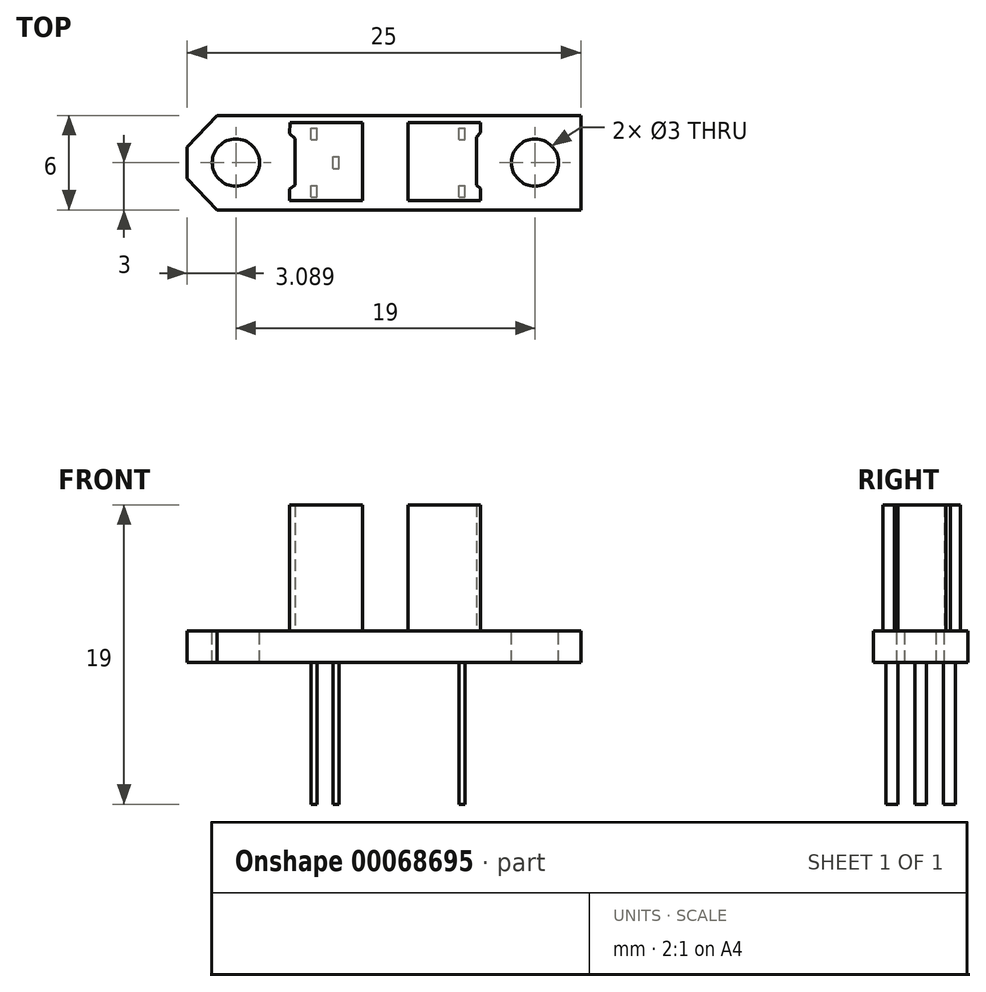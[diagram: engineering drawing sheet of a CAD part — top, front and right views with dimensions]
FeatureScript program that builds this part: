
annotation { "Feature Type Name" : "Feature", "Feature Type Description" : "" }
export const myFeature = defineFeature(function(context is Context, id is Id, definition is map)
    precondition{}
    {
        {
            var Q0;
            Q0=qCreatedBy(makeId("Top.planeOp"),FACE);
            var sketch = newSketch(context, id + "F0", { "sketchPlane" : qUnion([Q0])});
            skLineSegment(sketch, "E0.bottom", {"start": v(-23.1, 3) * mm, "end": v(0, 3) * mm});
            skLineSegment(sketch, "E0.top", {"start": v(-23.1, -3) * mm, "end": v(0, -3) * mm});
            skLineSegment(sketch, "E0.right", {"start": v(0, 3) * mm, "end": v(0, -3) * mm});
            skLineSegment(sketch, "E1", {"start": v(-23.1, 3) * mm, "end": v(-25, 1) * mm});
            skLineSegment(sketch, "E2", {"start": v(-25, 1) * mm, "end": v(-25, -1) * mm});
            skLineSegment(sketch, "E3", {"start": v(-25, -1) * mm, "end": v(-23.1, -3) * mm});
            skCircle(sketch, "E4", {"center": v(-21.91, 0) * mm, "radius": 1.5 * mm});
            skCircle(sketch, "E5", {"center": v(-2.91, 0) * mm, "radius": 1.5 * mm});
            skLineSegment(sketch, "E6", {"start": v(-18.47, 2.54) * mm, "end": v(-13.86, 2.54) * mm});
            skLineSegment(sketch, "E7", {"start": v(-13.86, 2.54) * mm, "end": v(-13.86, -2.4) * mm});
            skLineSegment(sketch, "E8", {"start": v(-13.86, -2.4) * mm, "end": v(-18.5, -2.4) * mm});
            skLineSegment(sketch, "E9", {"start": v(-18.5, -2.4) * mm, "end": v(-18.5, -1.68) * mm});
            skLineSegment(sketch, "E10", {"start": v(-18.5, -1.68) * mm, "end": v(-18.14, -1.41) * mm});
            skLineSegment(sketch, "E11", {"start": v(-18.14, -1.41) * mm, "end": v(-18.14, 1.53) * mm});
            skLineSegment(sketch, "E12", {"start": v(-18.14, 1.53) * mm, "end": v(-18.5, 1.86) * mm});
            skLineSegment(sketch, "E13", {"start": v(-18.5, 1.86) * mm, "end": v(-18.47, 2.54) * mm});
            skLineSegment(sketch, "E14", {"start": v(-10.98, 2.54) * mm, "end": v(-10.98, -2.4) * mm});
            skLineSegment(sketch, "E15", {"start": v(-10.98, -2.4) * mm, "end": v(-6.37, -2.4) * mm});
            skLineSegment(sketch, "E16", {"start": v(-6.37, -2.4) * mm, "end": v(-6.37, -1.65) * mm});
            skLineSegment(sketch, "E17", {"start": v(-6.37, -1.65) * mm, "end": v(-6.62, -1.43) * mm});
            skLineSegment(sketch, "E18", {"start": v(-6.62, -1.43) * mm, "end": v(-6.62, 1.62) * mm});
            skLineSegment(sketch, "E19", {"start": v(-6.62, 1.62) * mm, "end": v(-6.37, 1.9) * mm});
            skLineSegment(sketch, "E20", {"start": v(-6.37, 1.9) * mm, "end": v(-6.37, 2.54) * mm});
            skLineSegment(sketch, "E21", {"start": v(-6.37, 2.54) * mm, "end": v(-10.98, 2.54) * mm});
            skSolve(sketch);
        }
        {
            var Q0;
            Q0=makeQuery(id+"F0.imprint","IMPRINT",FACE,{"disambiguationData":[TD([[makeQuery(id+"F0.imprint","IMPRINT",EDGE,{"derivedFrom":sQuery(id+"F0.wireOp",EDGE,"E0.bottom")}),-1.0]])]});
            var Q1;
            Q1=makeQuery(id+"F0.imprint","IMPRINT",FACE,{"disambiguationData":[TD([[makeQuery(id+"F0.imprint","IMPRINT",EDGE,{"derivedFrom":sQuery(id+"F0.wireOp",EDGE,"E6")}),-1.0]])]});
            var Q2;
            Q2=makeQuery(id+"F0.imprint","IMPRINT",FACE,{"disambiguationData":[TD([[makeQuery(id+"F0.imprint","IMPRINT",EDGE,{"derivedFrom":sQuery(id+"F0.wireOp",EDGE,"E14")}),1.0]])]});
            extrude(context, id + "F1", {"entities" : qUnion([Q0, Q1, Q2]), "oppositeDirection" : true, "depth" : 2 * mm});
        }
        {
            var Q0;
            Q0=makeQuery(id+"F0.imprint","IMPRINT",FACE,{"disambiguationData":[TD([[makeQuery(id+"F0.imprint","IMPRINT",EDGE,{"derivedFrom":sQuery(id+"F0.wireOp",EDGE,"E6")}),-1.0]])]});
            var Q1;
            Q1=makeQuery(id+"F0.imprint","IMPRINT",FACE,{"disambiguationData":[TD([[makeQuery(id+"F0.imprint","IMPRINT",EDGE,{"derivedFrom":sQuery(id+"F0.wireOp",EDGE,"E14")}),1.0]])]});
            extrude(context, id + "F2", {"entities" : qUnion([Q0, Q1]), "operationType" : NewBodyOperationType.ADD, "depth" : 8 * mm});
        }
        {
            var Q0;
            Q0=makeQuery(id+"F1.opExtrude","CAP_FACE",FACE,{"disambiguationData":[OSD([sQuery(id+"F0.wireOp",EDGE,"E0.bottom"),sQuery(id+"F0.wireOp",EDGE,"E0.top"),sQuery(id+"F0.wireOp",EDGE,"E0.right"),sQuery(id+"F0.wireOp",EDGE,"E1"),sQuery(id+"F0.wireOp",EDGE,"E2"),sQuery(id+"F0.wireOp",EDGE,"E3"),sQuery(id+"F0.wireOp",EDGE,"E4"),sQuery(id+"F0.wireOp",EDGE,"E5")])],"isStart":false});
            var sketch = newSketch(context, id + "F3", { "sketchPlane" : qUnion([Q0])});
            skLineSegment(sketch, "E22.bottom", {"start": v(-17.15, 2.2) * mm, "end": v(-16.75, 2.2) * mm});
            skLineSegment(sketch, "E22.top", {"start": v(-17.15, 1.45) * mm, "end": v(-16.75, 1.45) * mm});
            skLineSegment(sketch, "E22.left", {"start": v(-17.15, 2.2) * mm, "end": v(-17.15, 1.45) * mm});
            skLineSegment(sketch, "E22.right", {"start": v(-16.75, 2.2) * mm, "end": v(-16.75, 1.45) * mm});
            skLineSegment(sketch, "E23.bottom", {"start": v(-15.75, 0.38) * mm, "end": v(-15.35, 0.38) * mm});
            skLineSegment(sketch, "E23.top", {"start": v(-15.75, -0.37) * mm, "end": v(-15.35, -0.37) * mm});
            skLineSegment(sketch, "E23.left", {"start": v(-15.75, 0.38) * mm, "end": v(-15.75, -0.37) * mm});
            skLineSegment(sketch, "E23.right", {"start": v(-15.35, 0.38) * mm, "end": v(-15.35, -0.37) * mm});
            skLineSegment(sketch, "E24.1.0.0", {"start": v(-7.75, 2.2) * mm, "end": v(-7.35, 2.2) * mm});
            skLineSegment(sketch, "E24.1.0.1", {"start": v(-7.35, 2.2) * mm, "end": v(-7.35, 1.45) * mm});
            skLineSegment(sketch, "E24.1.0.2", {"start": v(-7.75, 1.45) * mm, "end": v(-7.35, 1.45) * mm});
            skLineSegment(sketch, "E24.1.0.3", {"start": v(-7.75, 2.2) * mm, "end": v(-7.75, 1.45) * mm});
            skLineSegment(sketch, "E24.direction1", {"start": v(-17.15, 2.2) * mm, "end": v(-7.75, 2.2) * mm, "construction": true});
            skLineSegment(sketch, "E25.bottom", {"start": v(-17.15, -1.45) * mm, "end": v(-16.75, -1.45) * mm});
            skLineSegment(sketch, "E25.top", {"start": v(-17.15, -2.2) * mm, "end": v(-16.75, -2.2) * mm});
            skLineSegment(sketch, "E25.left", {"start": v(-17.15, -1.45) * mm, "end": v(-17.15, -2.2) * mm});
            skLineSegment(sketch, "E25.right", {"start": v(-16.75, -1.45) * mm, "end": v(-16.75, -2.2) * mm});
            skLineSegment(sketch, "E26.1.0.0", {"start": v(-7.75, -1.45) * mm, "end": v(-7.35, -1.45) * mm});
            skLineSegment(sketch, "E26.1.0.1", {"start": v(-7.75, -1.45) * mm, "end": v(-7.75, -2.2) * mm});
            skLineSegment(sketch, "E26.1.0.2", {"start": v(-7.35, -1.45) * mm, "end": v(-7.35, -2.2) * mm});
            skLineSegment(sketch, "E26.1.0.3", {"start": v(-7.75, -2.2) * mm, "end": v(-7.35, -2.2) * mm});
            skLineSegment(sketch, "E26.direction1", {"start": v(-17.15, -1.45) * mm, "end": v(-7.75, -1.45) * mm, "construction": true});
            skSolve(sketch);
        }
        {
            var Q0;
            Q0 = qSketchRegion(id + "F3", true);
            extrude(context, id + "F4", {"entities" : qUnion([Q0]), "depth" : 9 * mm});
        }
    });
